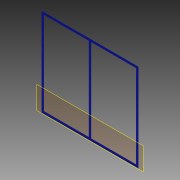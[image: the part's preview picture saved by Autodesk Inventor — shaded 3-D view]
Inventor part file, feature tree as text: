
AUTODESK INVENTOR PART (.ipt)
format: ipt  version: 2013 (Build 170138000, 138)  size: 84,480 bytes
history: native  units: in
note: dims shown in document units (in); Inventor stores cm internally (conversion verified against a paired STEP export)
features: plane x1, extrude x1, sketch x1, reference x1
ambient origin geometry x8: Origin, YZ Plane, XZ Plane, XY Plane, X Axis, Y Axis, Z Axis, Center Point
feature tree (4):
  plane  "Work Plane2"
  extrude  "Extrusion2"  Depth=2.0in
  sketch  "Sketch2"  dims[d8=2.0in d10=0.1in d11=0.0in d12=2.0in d13=1.0in]
  reference  "Reference4"
